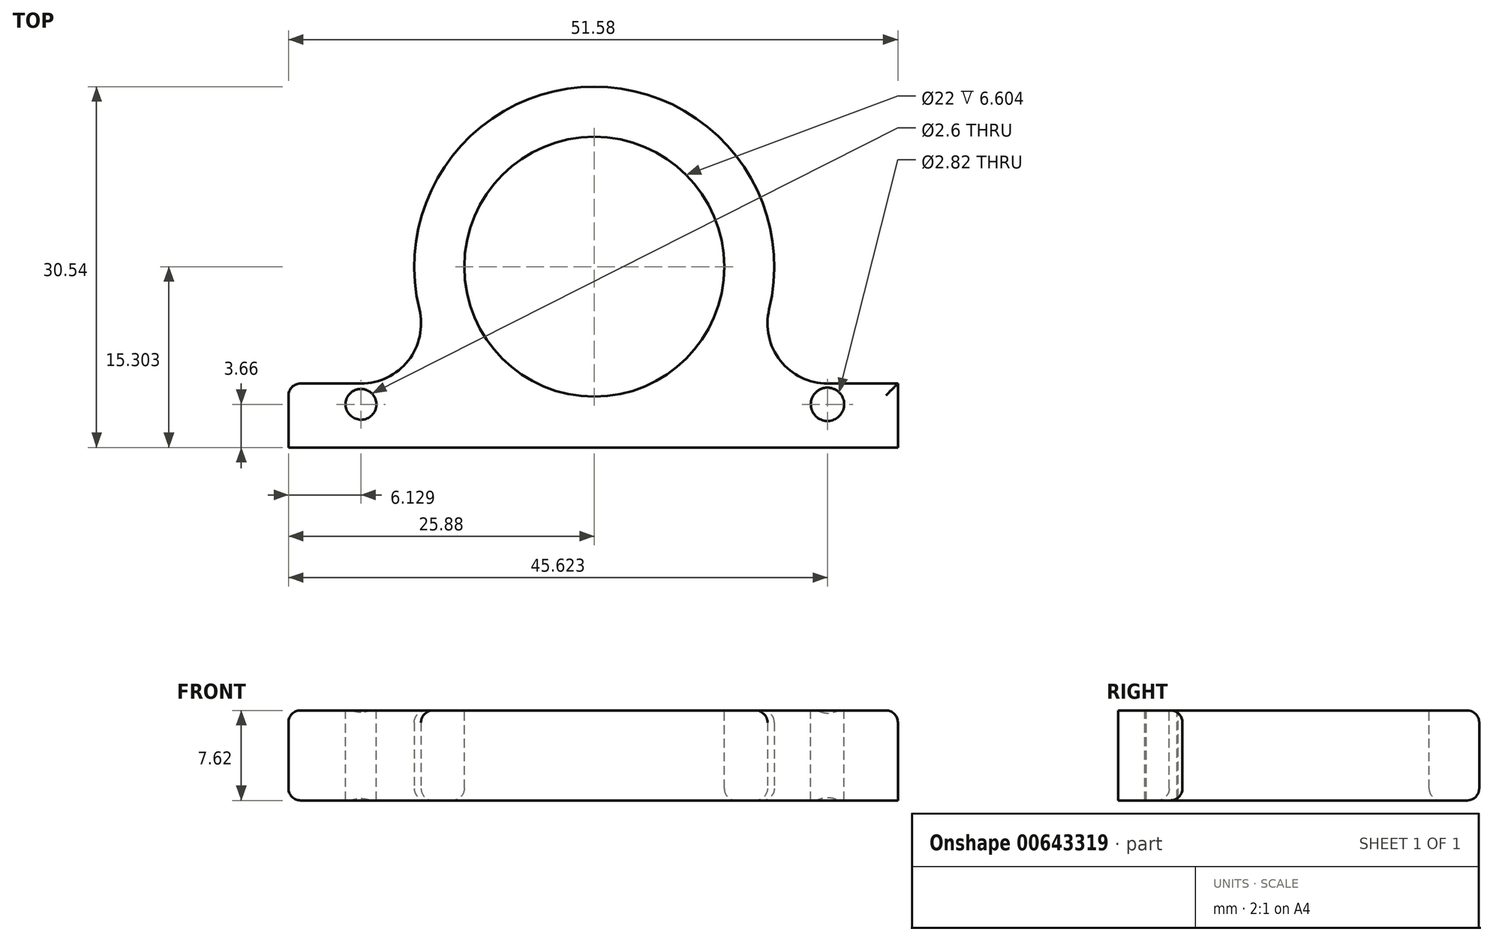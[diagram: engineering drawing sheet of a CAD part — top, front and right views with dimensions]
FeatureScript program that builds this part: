
annotation { "Feature Type Name" : "Feature", "Feature Type Description" : "" }
export const myFeature = defineFeature(function(context is Context, id is Id, definition is map)
    precondition{}
    {
        {
            var Q0;
            Q0=qCreatedBy(makeId("Top.planeOp"),FACE);
            var sketch = newSketch(context, id + "F0", { "sketchPlane" : qUnion([Q0])});
            skCircle(sketch, "E0", {"center": v(0, 11.64) * mm, "radius": 15.24 * mm});
            skLineSegment(sketch, "E1.bottom", {"start": v(-25.88, 1.76) * mm, "end": v(25.7, 1.76) * mm});
            skLineSegment(sketch, "E1.top", {"start": v(-25.88, -3.66) * mm, "end": v(25.7, -3.66) * mm});
            skLineSegment(sketch, "E1.left", {"start": v(-25.88, 1.76) * mm, "end": v(-25.88, -3.66) * mm});
            skLineSegment(sketch, "E1.right", {"start": v(25.7, 1.76) * mm, "end": v(25.7, -3.66) * mm});
            skSolve(sketch);
        }
        {
            var Q0;
            Q0=makeQuery(id+"F0.imprint","IMPRINT",FACE,{"disambiguationData":[TD([[makeQuery(id+"F0.imprint","IMPRINT",EDGE,{"derivedFrom":sQuery(id+"F0.wireOp",EDGE,"E1.top")}),1.0]])]});
            var Q1;
            {var subQ0=sQuery(id+"F0.wireOp",EDGE,"E1.bottom");var subQ1=sQuery(id+"F0.wireOp",EDGE,"E0");var subQ2=makeQuery(id+"F0.imprint","INTERSECT",VERTEX,{"disambiguationData":[OD(0.0)],"derivedFrom":[subQ1,subQ0]});Q1=makeQuery(id+"F0.imprint","IMPRINT",FACE,{"disambiguationData":[TD([[makeQuery(id+"F0.imprint","IMPRINT",EDGE,{"disambiguationData":[TD([[subQ2,-1.0]])],"derivedFrom":subQ1}),1.0]])]});}
            var Q2;
            {var subQ0=sQuery(id+"F0.wireOp",EDGE,"E1.bottom");var subQ1=sQuery(id+"F0.wireOp",EDGE,"E0");var subQ2=makeQuery(id+"F0.imprint","INTERSECT",VERTEX,{"disambiguationData":[OD(0.0)],"derivedFrom":[subQ1,subQ0]});Q2=makeQuery(id+"F0.imprint","IMPRINT",FACE,{"disambiguationData":[TD([[makeQuery(id+"F0.imprint","IMPRINT",EDGE,{"disambiguationData":[TD([[subQ2,1.0]])],"derivedFrom":subQ1}),1.0]])]});}
            extrude(context, id + "F1", {"entities" : qUnion([Q0, Q1, Q2]), "depth" : 7.62 * mm, "offsetDistance" : 25.4 * mm});
        }
        {
            var Q0;
            Q0=makeQuery(id+"F1.opExtrude","CAP_FACE",FACE,{"disambiguationData":[OSD([sQuery(id+"F0.wireOp",EDGE,"E0"),sQuery(id+"F0.wireOp",EDGE,"E1.bottom"),sQuery(id+"F0.wireOp",EDGE,"E1.top"),sQuery(id+"F0.wireOp",EDGE,"E1.left"),sQuery(id+"F0.wireOp",EDGE,"E1.right")])],"isStart":false});
            var sketch = newSketch(context, id + "F2", { "sketchPlane" : qUnion([Q0])});
            skCircle(sketch, "E2", {"center": v(0, 11.64) * mm, "radius": 11 * mm});
            skSolve(sketch);
        }
        {
            var Q0;
            Q0=makeQuery(id+"F2.imprint","IMPRINT",FACE,{"disambiguationData":[TD([[makeQuery(id+"F2.imprint","IMPRINT",EDGE,{"derivedFrom":sQuery(id+"F2.wireOp",EDGE,"E2")}),1.0]])]});
            extrude(context, id + "F3", {"entities" : qUnion([Q0]), "operationType" : NewBodyOperationType.REMOVE, "oppositeDirection" : true, "depth" : 25.4 * mm, "offsetDistance" : 25.4 * mm});
        }
        {
            var Q0;
            {var subQ0=sQuery(id+"F0.wireOp",EDGE,"E1.bottom");var subQ1=sQuery(id+"F0.wireOp",EDGE,"E0");Q0=makeQuery(id+"F1.opExtrude","SWEPT_EDGE",EDGE,{"disambiguationData":[OSD([subQ1,subQ0]),TDD([makeQuery(id+"F0.imprint","INTERSECT",VERTEX,{"disambiguationData":[OD(1.0)],"derivedFrom":[subQ1,subQ0]})])]});}
            var Q1;
            {var subQ0=sQuery(id+"F0.wireOp",EDGE,"E1.bottom");var subQ1=sQuery(id+"F0.wireOp",EDGE,"E0");Q1=makeQuery(id+"F1.opExtrude","SWEPT_EDGE",EDGE,{"disambiguationData":[OSD([subQ1,subQ0]),TDD([makeQuery(id+"F0.imprint","INTERSECT",VERTEX,{"disambiguationData":[OD(0.0)],"derivedFrom":[subQ1,subQ0]})])]});}
            fillet(context, id + "F4", {"entities" : qUnion([Q0, Q1]), "radius" : 5.08 * mm, "tangentPropagation" : true, "allowEdgeOverflow" : false});
        }
        {
            var Q0;
            {var subQ0=sQuery(id+"F0.wireOp",EDGE,"E1.bottom");Q0=makeQuery(id+"F1.opExtrude","CAP_EDGE",EDGE,{"disambiguationData":[OSD([subQ0]),TDD([makeQuery(id+"F0.imprint","IMPRINT",EDGE,{"disambiguationData":[TD([[makeQuery(id+"F0.imprint","INTERSECT",VERTEX,{"derivedFrom":[subQ0,sQuery(id+"F0.wireOp",EDGE,"E1.right")]}),1.0]])],"derivedFrom":subQ0})])],"isStart":false});}
            var Q1;
            Q1=makeQuery(id+"F1.opExtrude","CAP_EDGE",EDGE,{"disambiguationData":[OSD([sQuery(id+"F0.wireOp",EDGE,"E1.right")])],"isStart":false});
            var Q2;
            Q2=makeQuery(id+"F1.opExtrude","CAP_EDGE",EDGE,{"disambiguationData":[OSD([sQuery(id+"F0.wireOp",EDGE,"E1.left")])],"isStart":false});
            var Q3;
            Q3=makeQuery(id+"F1.opExtrude","CAP_EDGE",EDGE,{"disambiguationData":[OSD([sQuery(id+"F0.wireOp",EDGE,"E1.left")])],"isStart":true});
            var Q4;
            Q4=makeQuery(id+"F1.opExtrude","SWEPT_EDGE",EDGE,{"disambiguationData":[OSD([sQuery(id+"F0.wireOp",EDGE,"E1.bottom"),sQuery(id+"F0.wireOp",EDGE,"E1.left")])]});
            var Q5;
            {var subQ0=sQuery(id+"F0.wireOp",EDGE,"E1.bottom");var subQ1=sQuery(id+"F0.wireOp",EDGE,"E0");Q5=makeQuery(id+"F4.opFillet","BLEND_EDGE",EDGE,{"blendedFrom":[makeQuery(id+"F1.opExtrude","SWEPT_EDGE",EDGE,{"disambiguationData":[OSD([subQ1,subQ0]),TDD([makeQuery(id+"F0.imprint","INTERSECT",VERTEX,{"disambiguationData":[OD(0.0)],"derivedFrom":[subQ1,subQ0]})])]}),makeQuery(id+"F1.opExtrude","CAP_FACE",FACE,{"disambiguationData":[OSD([subQ1,subQ0,sQuery(id+"F0.wireOp",EDGE,"E1.top"),sQuery(id+"F0.wireOp",EDGE,"E1.left"),sQuery(id+"F0.wireOp",EDGE,"E1.right")])],"isStart":true})],"blendedInto":[makeQuery(id+"F1.opExtrude","CAP_FACE",FACE,{"disambiguationData":[OSD([subQ1,subQ0,sQuery(id+"F0.wireOp",EDGE,"E1.top"),sQuery(id+"F0.wireOp",EDGE,"E1.left"),sQuery(id+"F0.wireOp",EDGE,"E1.right")])],"isStart":true})]});}
            var Q6;
            Q6=makeQuery(id+"F3.boolean.opBoolean","INTERSECT",EDGE,{"derivedFrom":[makeQuery(id+"F1.opExtrude","CAP_FACE",FACE,{"disambiguationData":[OSD([sQuery(id+"F0.wireOp",EDGE,"E0"),sQuery(id+"F0.wireOp",EDGE,"E1.bottom"),sQuery(id+"F0.wireOp",EDGE,"E1.top"),sQuery(id+"F0.wireOp",EDGE,"E1.left"),sQuery(id+"F0.wireOp",EDGE,"E1.right")])],"isStart":true}),makeQuery(id+"F3.opExtrude","SWEPT_FACE",FACE,{"disambiguationData":[OSD([sQuery(id+"F2.wireOp",EDGE,"E2")])]})]});
            var Q7;
            Q7=makeQuery(id+"F3.boolean.opBoolean","COPY",EDGE,{"derivedFrom":makeQuery(id+"F3.opExtrude","CAP_EDGE",EDGE,{"disambiguationData":[OSD([sQuery(id+"F2.wireOp",EDGE,"E2")])],"isStart":true})});
            fillet(context, id + "F5", {"entities" : qUnion([Q0, Q1, Q2, Q3, Q4, Q5, Q6, Q7]), "radius" : 1.02 * mm, "tangentPropagation" : true, "allowEdgeOverflow" : false});
        }
        {
            var Q0;
            Q0=makeQuery(id+"F1.opExtrude","CAP_FACE",FACE,{"disambiguationData":[OSD([sQuery(id+"F0.wireOp",EDGE,"E0"),sQuery(id+"F0.wireOp",EDGE,"E1.bottom"),sQuery(id+"F0.wireOp",EDGE,"E1.top"),sQuery(id+"F0.wireOp",EDGE,"E1.left"),sQuery(id+"F0.wireOp",EDGE,"E1.right")])],"isStart":false});
            var sketch = newSketch(context, id + "F6", { "sketchPlane" : qUnion([Q0])});
            skCircle(sketch, "E3", {"center": v(-19.75, 0) * mm, "radius": 1.3 * mm});
            skCircle(sketch, "E4", {"center": v(19.74, 0) * mm, "radius": 1.41 * mm});
            skSolve(sketch);
        }
        {
            var Q0;
            {var subQ0=sQuery(id+"F6.wireOp",EDGE,"E3");var subQ1=sQuery(id+"F0.wireOp",EDGE,"E1.left");var subQ2=sQuery(id+"F0.wireOp",EDGE,"E1.bottom");var subQ3=sQuery(id+"F0.wireOp",EDGE,"E0");var subQ4=makeQuery(id+"F1.opExtrude","CAP_FACE",FACE,{"disambiguationData":[OSD([subQ3,subQ2,sQuery(id+"F0.wireOp",EDGE,"E1.top"),subQ1,sQuery(id+"F0.wireOp",EDGE,"E1.right")])],"isStart":false});var subQ5=subQ4;var subQ9=makeQuery(id+"F5.opFillet","BLEND_EDGE",EDGE,{"blendedFrom":[makeQuery(id+"F1.opExtrude","CAP_EDGE",EDGE,{"disambiguationData":[OSD([subQ2]),TDD([makeQuery(id+"F0.imprint","IMPRINT",EDGE,{"disambiguationData":[TD([[makeQuery(id+"F0.imprint","INTERSECT",VERTEX,{"derivedFrom":[subQ2,subQ1]}),-1.0]])],"derivedFrom":subQ2})])],"isStart":false}),subQ5],"blendedInto":[subQ5]});var subQ10=makeQuery(id+"F6.imprint","INTERSECT",VERTEX,{"derivedFrom":[subQ9,subQ0]});Q0=makeQuery(id+"F6.imprint","IMPRINT",FACE,{"disambiguationData":[TD([[makeQuery(id+"F6.imprint","IMPRINT",EDGE,{"disambiguationData":[TD([[subQ10,-1.0]])],"derivedFrom":subQ0}),1.0]])]});}
            var Q1;
            {var subQ0=sQuery(id+"F6.wireOp",EDGE,"E3");var subQ1=sQuery(id+"F0.wireOp",EDGE,"E1.left");var subQ2=sQuery(id+"F0.wireOp",EDGE,"E1.bottom");var subQ3=sQuery(id+"F0.wireOp",EDGE,"E0");var subQ4=makeQuery(id+"F1.opExtrude","CAP_FACE",FACE,{"disambiguationData":[OSD([subQ3,subQ2,sQuery(id+"F0.wireOp",EDGE,"E1.top"),subQ1,sQuery(id+"F0.wireOp",EDGE,"E1.right")])],"isStart":false});var subQ5=subQ4;var subQ9=makeQuery(id+"F5.opFillet","BLEND_EDGE",EDGE,{"blendedFrom":[makeQuery(id+"F1.opExtrude","CAP_EDGE",EDGE,{"disambiguationData":[OSD([subQ2]),TDD([makeQuery(id+"F0.imprint","IMPRINT",EDGE,{"disambiguationData":[TD([[makeQuery(id+"F0.imprint","INTERSECT",VERTEX,{"derivedFrom":[subQ2,subQ1]}),-1.0]])],"derivedFrom":subQ2})])],"isStart":false}),subQ5],"blendedInto":[subQ5]});var subQ10=makeQuery(id+"F6.imprint","INTERSECT",VERTEX,{"derivedFrom":[subQ9,subQ0]});Q1=makeQuery(id+"F6.imprint","IMPRINT",FACE,{"disambiguationData":[TD([[makeQuery(id+"F6.imprint","IMPRINT",EDGE,{"disambiguationData":[TD([[subQ10,1.0]])],"derivedFrom":subQ0}),1.0]])]});}
            var Q2;
            {var subQ0=sQuery(id+"F6.wireOp",EDGE,"E4");var subQ1=sQuery(id+"F0.wireOp",EDGE,"E1.right");var subQ2=sQuery(id+"F0.wireOp",EDGE,"E1.bottom");var subQ3=sQuery(id+"F0.wireOp",EDGE,"E0");var subQ4=makeQuery(id+"F1.opExtrude","CAP_FACE",FACE,{"disambiguationData":[OSD([subQ3,subQ2,sQuery(id+"F0.wireOp",EDGE,"E1.top"),sQuery(id+"F0.wireOp",EDGE,"E1.left"),subQ1])],"isStart":false});var subQ5=subQ4;var subQ9=makeQuery(id+"F5.opFillet","BLEND_EDGE",EDGE,{"blendedFrom":[makeQuery(id+"F1.opExtrude","CAP_EDGE",EDGE,{"disambiguationData":[OSD([subQ2]),TDD([makeQuery(id+"F0.imprint","IMPRINT",EDGE,{"disambiguationData":[TD([[makeQuery(id+"F0.imprint","INTERSECT",VERTEX,{"derivedFrom":[subQ2,subQ1]}),1.0]])],"derivedFrom":subQ2})])],"isStart":false}),subQ5],"blendedInto":[subQ5]});var subQ10=makeQuery(id+"F6.imprint","INTERSECT",VERTEX,{"derivedFrom":[subQ9,subQ0]});Q2=makeQuery(id+"F6.imprint","IMPRINT",FACE,{"disambiguationData":[TD([[makeQuery(id+"F6.imprint","IMPRINT",EDGE,{"disambiguationData":[TD([[subQ10,1.0]])],"derivedFrom":subQ0}),1.0]])]});}
            var Q3;
            {var subQ0=sQuery(id+"F6.wireOp",EDGE,"E4");var subQ1=sQuery(id+"F0.wireOp",EDGE,"E1.right");var subQ2=sQuery(id+"F0.wireOp",EDGE,"E1.bottom");var subQ3=sQuery(id+"F0.wireOp",EDGE,"E0");var subQ4=makeQuery(id+"F1.opExtrude","CAP_FACE",FACE,{"disambiguationData":[OSD([subQ3,subQ2,sQuery(id+"F0.wireOp",EDGE,"E1.top"),sQuery(id+"F0.wireOp",EDGE,"E1.left"),subQ1])],"isStart":false});var subQ5=subQ4;var subQ9=makeQuery(id+"F5.opFillet","BLEND_EDGE",EDGE,{"blendedFrom":[makeQuery(id+"F1.opExtrude","CAP_EDGE",EDGE,{"disambiguationData":[OSD([subQ2]),TDD([makeQuery(id+"F0.imprint","IMPRINT",EDGE,{"disambiguationData":[TD([[makeQuery(id+"F0.imprint","INTERSECT",VERTEX,{"derivedFrom":[subQ2,subQ1]}),1.0]])],"derivedFrom":subQ2})])],"isStart":false}),subQ5],"blendedInto":[subQ5]});var subQ10=makeQuery(id+"F6.imprint","INTERSECT",VERTEX,{"derivedFrom":[subQ9,subQ0]});Q3=makeQuery(id+"F6.imprint","IMPRINT",FACE,{"disambiguationData":[TD([[makeQuery(id+"F6.imprint","IMPRINT",EDGE,{"disambiguationData":[TD([[subQ10,-1.0]])],"derivedFrom":subQ0}),1.0]])]});}
            extrude(context, id + "F7", {"entities" : qUnion([Q0, Q1, Q2, Q3]), "operationType" : NewBodyOperationType.REMOVE, "oppositeDirection" : true, "depth" : 25.4 * mm, "offsetDistance" : 25.4 * mm});
        }
    });
